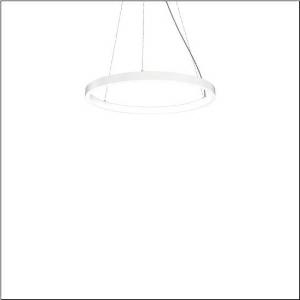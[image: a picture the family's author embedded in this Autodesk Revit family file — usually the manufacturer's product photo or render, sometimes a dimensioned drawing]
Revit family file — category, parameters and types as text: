
# Revit family: silica_21_ring-i_5pjbi2d3004a
name_source: partatom
category: Lighting Fixtures
units: mm (PartAtom-declared; Revit-internal decimal feet)

## family parameters
Cut with Voids When Loaded = No
Host = Face
Light Source = No
Part Type = Normal
Room Calculation Point = No
Round Connector Dimension = Use Diameter
Shared = No

## types (1)
- Silica 21 Ring-I (1 x LED, 5040 lm, 80 W, 4000K)
    Apparent Load = 80 VA
    CIE Flux Codes = 22 48 76 50 101
    Color Rendering = 80
    Color Temperature = 4000K
    Default Elevation = 1800 mm
    Description = Silica 21 Ring-I, suspended luminaire, of PMMA, frosted, light emission: inner ring side luminous distribution, primary light characteristic: symmetric, installation type: suspended mounting, LED, rated luminous flux: 5.040lm, luminous efficacy: 63lm/W, light colour: 840, colour temperature: 4000K, control gear: DALI 2, with terminal, 5-pole, mains connection: 230V, AC/DC, 0/50..60Hz, rated input power: 80W, housing, of extruded aluminium section, traffic white (RAL 9016), diameter: 805mm, ceiling canopy, traffic white (RAL 9016), protection rating (lamp compartment): IP40, insulation class (complete): insulation class I (protective earthing), certification: CE, impact resistance: IK02, permissible operating ambient temperature: 0..+35°C, packaging unit: 1 piece
    Height = 48 mm  [stored 0.15748 ft]
    Lamp = 1 x LED
    Lamp Light Flux = 5040 lm
    Lamp Power = 80 W
    Lamp count = 1
    Length = 805 mm
    Luminous efficacy = 63 lm/W
    Manufacturer = Siteco
    ModVariant = No
    Model = 5PJBI2D3004A
    Mounting Place = Ceiling
    Mounting Type = Pendant
    Number of Poles = 1
    OnlyDefault = Yes
    Power Factor = 1
    Product Name = Silica 21 Ring-I
    Product group = suspended luminaire
    ProductGroupID = 904
    Protection Class = Protection class I
    Protection Degree = IP 40
    RLX_Detail_Level = 1
    RLX_Emergency_Light_Flux = 0 lm
    RLX_Emergency_Type = 0
    RLX_Emergency_Type_DB = No
    RlxData = <blob elided: 11561 chars, md5=df1591ff>
    Socket = socket
    Standby Power = 0 W
    System Light Flux = 5040 lm
    System Power = 80 W
    Type Comments = Product without accessories
    Type Image = l_1258367.jpg
    URL = http://relux.com
    VarID = ---
    Voltage = 0 V
    Weight = 0.00 kg
    Width = 0 mm  [stored 0 ft]

note: [stored X ft] marks values corroborated as IEEE doubles in the binary element streams (Revit-internal decimal feet)

## geometry (parser evidence)
native form markers: Sweep x11
no freeform markers — native parametric forms only
